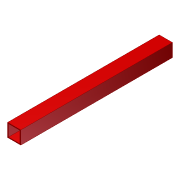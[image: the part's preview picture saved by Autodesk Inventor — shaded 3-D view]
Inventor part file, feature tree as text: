
AUTODESK INVENTOR PART (.ipt)
format: ipt  version: 2012 (Build 160160000, 160)  size: 74,752 bytes
history: native  units: in
note: dims shown in document units (in); Inventor stores cm internally (conversion verified against a paired STEP export)
features: extrude x1, shell x1, sketch x1
ambient origin geometry x8: Origin, YZ Plane, XZ Plane, XY Plane, X Axis, Y Axis, Z Axis, Center Point
bodies: Solid1 (feature_tree)
feature tree (3):
  extrude  "Extrusion1"  Depth=2.0in
  shell  "Shell1"  Thickness=18.0in
  sketch  "Sketch1"  dims[d0=2.0in d1=2.0in d2=18.0in d3=0.0in d4=0.125in]
